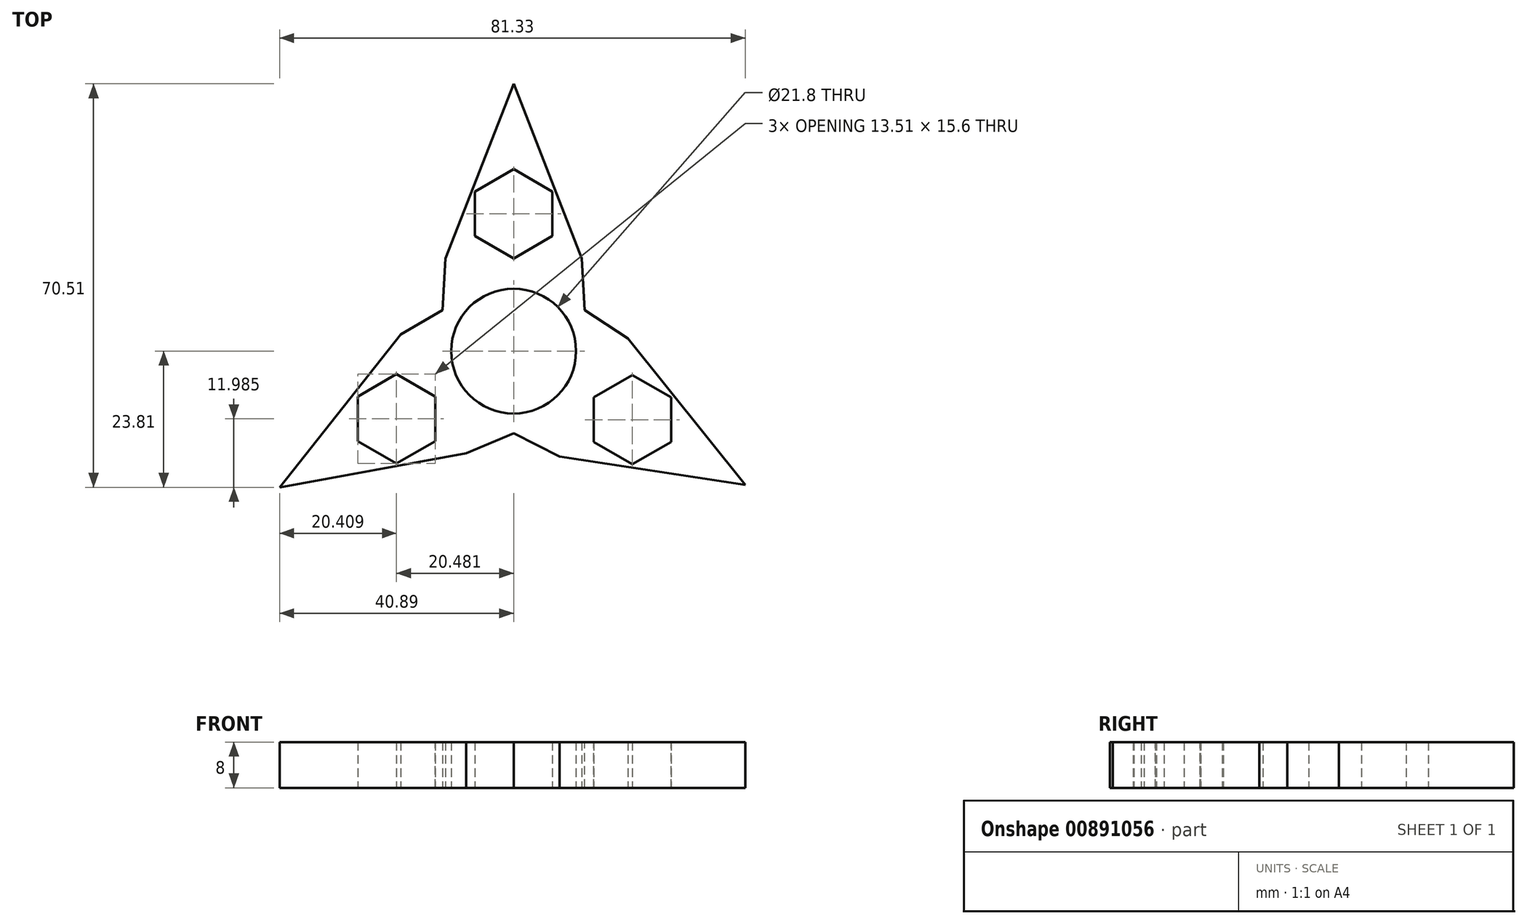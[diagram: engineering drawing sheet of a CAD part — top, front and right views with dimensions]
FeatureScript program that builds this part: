
annotation { "Feature Type Name" : "Feature", "Feature Type Description" : "" }
export const myFeature = defineFeature(function(context is Context, id is Id, definition is map)
    precondition{}
    {
        {
            var Q0;
            Q0=qCreatedBy(makeId("Top.planeOp"),FACE);
            var sketch = newSketch(context, id + "F0", { "sketchPlane" : qUnion([Q0])});
            skCircle(sketch, "E0", {"center": v(0, 0) * mm, "radius": 10.9 * mm});
            skPoint(sketch, "E1.end.orphan", {"position": v(-149.66, 6.75) * mm});
            skPoint(sketch, "E2.end.orphan", {"position": v(-152.03, 6.75) * mm});
            skCircle(sketch, "E3.cCircle", {"center": v(0, 24) * mm, "radius": 6.75 * mm, "construction": true});
            skLineSegment(sketch, "E3.0", {"start": v(6.75, 20.1) * mm, "end": v(0, 16.2) * mm});
            skLineSegment(sketch, "E3.1", {"start": v(0, 16.2) * mm, "end": v(-6.75, 20.1) * mm});
            skLineSegment(sketch, "E3.2", {"start": v(-6.75, 20.1) * mm, "end": v(-6.75, 27.9) * mm});
            skLineSegment(sketch, "E3.3", {"start": v(-6.75, 27.9) * mm, "end": v(0, 31.8) * mm});
            skLineSegment(sketch, "E3.4", {"start": v(0, 31.8) * mm, "end": v(6.75, 27.9) * mm});
            skLineSegment(sketch, "E3.5", {"start": v(6.75, 27.9) * mm, "end": v(6.75, 20.1) * mm});
            skPoint(sketch, "E3.0.midPoint", {"position": v(3.38, 18.15) * mm});
            skCircle(sketch, "E4.cCircle", {"center": v(20.75, -11.98) * mm, "radius": 6.75 * mm, "construction": true});
            skLineSegment(sketch, "E4.0", {"start": v(27.5, -8.08) * mm, "end": v(27.5, -15.88) * mm});
            skLineSegment(sketch, "E4.1", {"start": v(27.5, -15.88) * mm, "end": v(20.75, -19.78) * mm});
            skLineSegment(sketch, "E4.2", {"start": v(20.75, -19.78) * mm, "end": v(14, -15.88) * mm});
            skLineSegment(sketch, "E4.3", {"start": v(14, -15.88) * mm, "end": v(14, -8.08) * mm});
            skLineSegment(sketch, "E4.4", {"start": v(14, -8.08) * mm, "end": v(20.75, -4.18) * mm});
            skLineSegment(sketch, "E4.5", {"start": v(20.75, -4.18) * mm, "end": v(27.5, -8.08) * mm});
            skCircle(sketch, "E5.cCircle", {"center": v(-20.48, -11.82) * mm, "radius": 6.75 * mm, "construction": true});
            skLineSegment(sketch, "E5.0", {"start": v(-13.73, -7.92) * mm, "end": v(-13.73, -15.72) * mm});
            skLineSegment(sketch, "E5.1", {"start": v(-13.73, -15.72) * mm, "end": v(-20.48, -19.62) * mm});
            skLineSegment(sketch, "E5.2", {"start": v(-20.48, -19.62) * mm, "end": v(-27.24, -15.72) * mm});
            skLineSegment(sketch, "E5.3", {"start": v(-27.24, -15.72) * mm, "end": v(-27.24, -7.92) * mm});
            skLineSegment(sketch, "E5.4", {"start": v(-27.24, -7.92) * mm, "end": v(-20.48, -4.02) * mm});
            skLineSegment(sketch, "E5.5", {"start": v(-20.48, -4.02) * mm, "end": v(-13.73, -7.92) * mm});
            skArc(sketch, "E6.cCircle", {"start": v(-27.98, -8.35) * mm, "mid": v(-25.29, -14.6) * mm, "end": v(-21.22, -20.05) * mm, "construction": true});
            skPoint(sketch, "E7.orphan", {"position": v(3.83, 56.25) * mm});
            skArc(sketch, "E8.trimOffspring", {"start": v(6.75, 28.4) * mm, "mid": v(0, 29.2) * mm, "end": v(-6.75, 28.4) * mm, "construction": true});
            skArc(sketch, "E9.trimOffspring", {"start": v(21.22, -20.05) * mm, "mid": v(25.29, -14.6) * mm, "end": v(27.98, -8.35) * mm, "construction": true});
            skLineSegment(sketch, "E10", {"start": v(-20.48, -11.82) * mm, "end": v(0, 0) * mm});
            skLineSegment(sketch, "E11", {"start": v(0, 0) * mm, "end": v(20.75, -11.98) * mm});
            skLineSegment(sketch, "E12", {"start": v(20.75, -11.98) * mm, "end": v(40.44, -23.35) * mm});
            skLineSegment(sketch, "E13", {"start": v(8.03, -18.4) * mm, "end": v(40.44, -23.35) * mm});
            skLineSegment(sketch, "E14", {"start": v(0, -14.34) * mm, "end": v(8.03, -18.4) * mm});
            skLineSegment(sketch, "E15.MirrorCS", {"start": v(19.95, 2.24) * mm, "end": v(40.44, -23.35) * mm});
            skLineSegment(sketch, "E16.MirrorCS", {"start": v(12.42, 7.17) * mm, "end": v(19.95, 2.24) * mm});
            skLineSegment(sketch, "E17.MirrorCS", {"start": v(-12.42, 7.17) * mm, "end": v(-19.7, 2.9) * mm});
            skLineSegment(sketch, "E18.MirrorCS", {"start": v(-19.7, 2.9) * mm, "end": v(-40.89, -23.8) * mm});
            skLineSegment(sketch, "E19.MirrorCS", {"start": v(-8.27, -17.88) * mm, "end": v(-40.89, -23.8) * mm});
            skLineSegment(sketch, "E20.MirrorCS", {"start": v(20.75, -11.98) * mm, "end": v(0, 0) * mm});
            skLineSegment(sketch, "E21.MirrorCS", {"start": v(-12.42, 7.17) * mm, "end": v(-11.92, 16.16) * mm});
            skLineSegment(sketch, "E22.MirrorCS", {"start": v(-11.92, 16.16) * mm, "end": v(0, 46.7) * mm});
            skLineSegment(sketch, "E23.MirrorCS", {"start": v(11.92, 16.16) * mm, "end": v(0, 46.7) * mm});
            skLineSegment(sketch, "E24.MirrorCS", {"start": v(12.42, 7.17) * mm, "end": v(11.92, 16.16) * mm});
            skLineSegment(sketch, "E25", {"start": v(-8.27, -17.88) * mm, "end": v(0, -14.34) * mm});
            skSolve(sketch);
        }
        {
            var Q0;
            Q0 = qSketchRegion(id + "F0", true);
            extrude(context, id + "F1", {"entities" : qUnion([Q0]), "depth" : 8 * mm, "offsetDistance" : 25 * mm});
        }
    });
